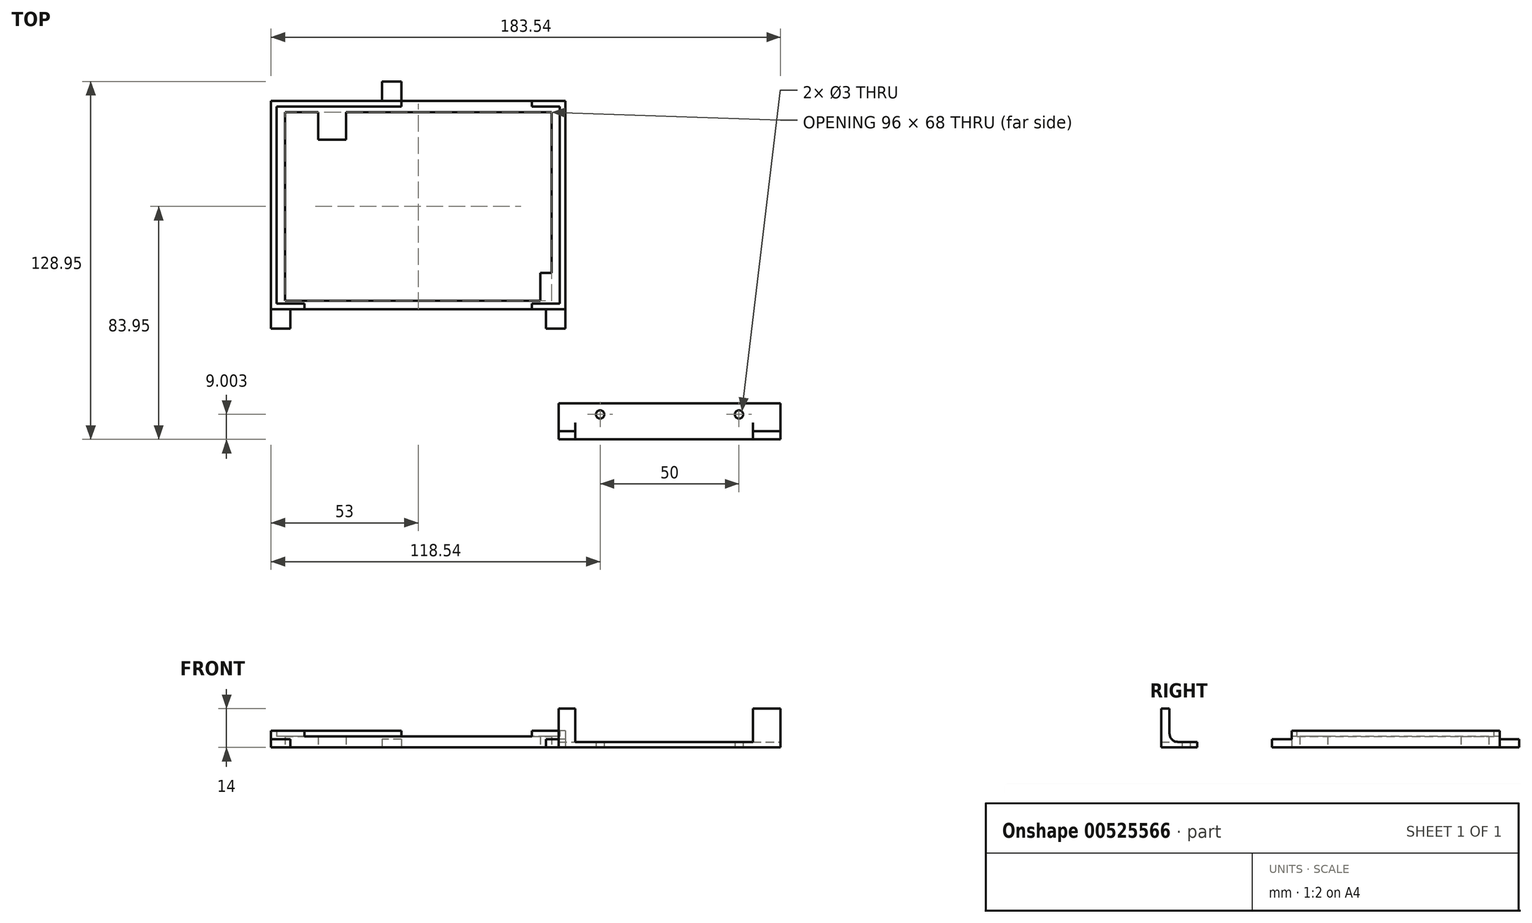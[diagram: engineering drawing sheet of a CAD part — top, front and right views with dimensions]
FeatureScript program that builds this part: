
annotation { "Feature Type Name" : "Feature", "Feature Type Description" : "" }
export const myFeature = defineFeature(function(context is Context, id is Id, definition is map)
    precondition{}
    {
        {
            var Q0;
            Q0=qCreatedBy(makeId("Top.planeOp"),FACE);
            var sketch = newSketch(context, id + "F0", { "sketchPlane" : qUnion([Q0])});
            skLineSegment(sketch, "E0.bottom", {"start": v(51, -35.5) * mm, "end": v(-51, -35.5) * mm});
            skLineSegment(sketch, "E0.top", {"start": v(51, 35.5) * mm, "end": v(-51, 35.5) * mm});
            skLineSegment(sketch, "E0.left", {"start": v(51, -35.5) * mm, "end": v(51, 35.5) * mm});
            skLineSegment(sketch, "E0.right", {"start": v(-51, -35.5) * mm, "end": v(-51, 35.5) * mm});
            skPoint(sketch, "E0.middle", {"position": v(0, 0) * mm});
            skLineSegment(sketch, "E1.bottom", {"start": v(53, -37.5) * mm, "end": v(-53, -37.5) * mm});
            skLineSegment(sketch, "E1.top", {"start": v(53, 37.5) * mm, "end": v(-53, 37.5) * mm});
            skLineSegment(sketch, "E1.left", {"start": v(53, -37.5) * mm, "end": v(53, 37.5) * mm});
            skLineSegment(sketch, "E1.right", {"start": v(-53, -37.5) * mm, "end": v(-53, 37.5) * mm});
            skSolve(sketch);
        }
        {
            var Q0;
            Q0=qSketchRegion(id+"F0",true);
            extrude(context, id + "F1", {"entities" : qUnion([Q0]), "depth" : 6 * mm, "offsetDistance" : 25 * mm});
        }
        {
            var Q0;
            Q0=makeQuery(id+"F1.opExtrude","CAP_FACE",FACE,{"disambiguationData":[OSD([sQuery(id+"F0.wireOp",EDGE,"E0.bottom"),sQuery(id+"F0.wireOp",EDGE,"E0.top"),sQuery(id+"F0.wireOp",EDGE,"E0.left"),sQuery(id+"F0.wireOp",EDGE,"E0.right"),sQuery(id+"F0.wireOp",EDGE,"E1.bottom"),sQuery(id+"F0.wireOp",EDGE,"E1.top"),sQuery(id+"F0.wireOp",EDGE,"E1.left"),sQuery(id+"F0.wireOp",EDGE,"E1.right")])],"isStart":true});
            var sketch = newSketch(context, id + "F2", { "sketchPlane" : qUnion([Q0])});
            skLineSegment(sketch, "E2.bottom", {"start": v(51, 35.5) * mm, "end": v(-51, 35.5) * mm});
            skLineSegment(sketch, "E2.top", {"start": v(51, -35.5) * mm, "end": v(-51, -35.5) * mm});
            skLineSegment(sketch, "E2.left", {"start": v(51, 35.5) * mm, "end": v(51, -35.5) * mm});
            skLineSegment(sketch, "E2.right", {"start": v(-51, 35.5) * mm, "end": v(-51, -35.5) * mm});
            skPoint(sketch, "E2.middle", {"position": v(0, 0) * mm});
            skLineSegment(sketch, "E3.bottom", {"start": v(-48, -33.5) * mm, "end": v(-36, -33.5) * mm});
            skLineSegment(sketch, "E3.top", {"start": v(-48, 34.5) * mm, "end": v(44, 34.5) * mm});
            skLineSegment(sketch, "E3.left", {"start": v(-48, -33.5) * mm, "end": v(-48, 34.5) * mm});
            skLineSegment(sketch, "E3.right", {"start": v(48, -33.5) * mm, "end": v(48, 24.5) * mm});
            skLineSegment(sketch, "E4", {"start": v(48, 24.5) * mm, "end": v(44, 24.5) * mm});
            skLineSegment(sketch, "E5", {"start": v(44, 24.5) * mm, "end": v(44, 34.5) * mm});
            skLineSegment(sketch, "E6", {"start": v(-36, -33.5) * mm, "end": v(-36, -23.5) * mm});
            skLineSegment(sketch, "E7", {"start": v(-36, -23.5) * mm, "end": v(-26, -23.5) * mm});
            skLineSegment(sketch, "E8", {"start": v(-26, -23.5) * mm, "end": v(-26, -33.5) * mm});
            skLineSegment(sketch, "E9.trimOffspring", {"start": v(-26, -33.5) * mm, "end": v(48, -33.5) * mm});
            skSolve(sketch);
        }
        {
            var Q0;
            Q0 = qSketchRegion(id + "F2", true);
            extrude(context, id + "F3", {"entities" : qUnion([Q0]), "operationType" : NewBodyOperationType.ADD, "oppositeDirection" : true, "depth" : 4 * mm, "offsetDistance" : 25 * mm});
        }
        {
            var Q0;
            Q0=makeQuery(id+"F1.opExtrude","CAP_FACE",FACE,{"disambiguationData":[OSD([sQuery(id+"F0.wireOp",EDGE,"E0.bottom"),sQuery(id+"F0.wireOp",EDGE,"E0.top"),sQuery(id+"F0.wireOp",EDGE,"E0.left"),sQuery(id+"F0.wireOp",EDGE,"E0.right"),sQuery(id+"F0.wireOp",EDGE,"E1.bottom"),sQuery(id+"F0.wireOp",EDGE,"E1.top"),sQuery(id+"F0.wireOp",EDGE,"E1.left"),sQuery(id+"F0.wireOp",EDGE,"E1.right")])],"isStart":false});
            var sketch = newSketch(context, id + "F4", { "sketchPlane" : qUnion([Q0])});
            skLineSegment(sketch, "E10.bottom", {"start": v(-41, -35.5) * mm, "end": v(41, -35.5) * mm});
            skLineSegment(sketch, "E10.top", {"start": v(-41, -37.5) * mm, "end": v(41, -37.5) * mm});
            skLineSegment(sketch, "E10.left", {"start": v(-41, -35.5) * mm, "end": v(-41, -37.5) * mm});
            skLineSegment(sketch, "E10.right", {"start": v(41, -35.5) * mm, "end": v(41, -37.5) * mm});
            skLineSegment(sketch, "E11.bottom", {"start": v(-6, 37.5) * mm, "end": v(41, 37.5) * mm});
            skLineSegment(sketch, "E11.top", {"start": v(-6, 35.5) * mm, "end": v(41, 35.5) * mm});
            skLineSegment(sketch, "E11.left", {"start": v(-6, 37.5) * mm, "end": v(-6, 35.5) * mm});
            skLineSegment(sketch, "E11.right", {"start": v(41, 37.5) * mm, "end": v(41, 35.5) * mm});
            skSolve(sketch);
        }
        {
            var Q0;
            Q0 = qSketchRegion(id + "F4", true);
            extrude(context, id + "F5", {"entities" : qUnion([Q0]), "operationType" : NewBodyOperationType.REMOVE, "oppositeDirection" : true, "depth" : 2 * mm, "offsetDistance" : 25 * mm});
        }
        {
            var Q0;
            Q0=makeQuery(id+"F3.boolean.opBoolean","MERGE",FACE,{"derivedFrom":[makeQuery(id+"F1.opExtrude","CAP_FACE",FACE,{"disambiguationData":[OSD([sQuery(id+"F0.wireOp",EDGE,"E0.bottom"),sQuery(id+"F0.wireOp",EDGE,"E0.top"),sQuery(id+"F0.wireOp",EDGE,"E0.left"),sQuery(id+"F0.wireOp",EDGE,"E0.right"),sQuery(id+"F0.wireOp",EDGE,"E1.bottom"),sQuery(id+"F0.wireOp",EDGE,"E1.top"),sQuery(id+"F0.wireOp",EDGE,"E1.left"),sQuery(id+"F0.wireOp",EDGE,"E1.right")])],"isStart":true}),makeQuery(id+"F3.opExtrude","CAP_FACE",FACE,{"disambiguationData":[OSD([sQuery(id+"F2.wireOp",EDGE,"E2.bottom"),sQuery(id+"F2.wireOp",EDGE,"E2.top"),sQuery(id+"F2.wireOp",EDGE,"E2.left"),sQuery(id+"F2.wireOp",EDGE,"E2.right"),sQuery(id+"F2.wireOp",EDGE,"E3.bottom"),sQuery(id+"F2.wireOp",EDGE,"E3.top"),sQuery(id+"F2.wireOp",EDGE,"E3.left"),sQuery(id+"F2.wireOp",EDGE,"E3.right"),sQuery(id+"F2.wireOp",EDGE,"E4"),sQuery(id+"F2.wireOp",EDGE,"E5"),sQuery(id+"F2.wireOp",EDGE,"E6"),sQuery(id+"F2.wireOp",EDGE,"E7"),sQuery(id+"F2.wireOp",EDGE,"E8"),sQuery(id+"F2.wireOp",EDGE,"E9.trimOffspring")])],"isStart":true})]});
            var sketch = newSketch(context, id + "F6", { "sketchPlane" : qUnion([Q0])});
            skLineSegment(sketch, "E12.bottom", {"start": v(53, 37.5) * mm, "end": v(46, 37.5) * mm});
            skLineSegment(sketch, "E12.top", {"start": v(53, 44.5) * mm, "end": v(46, 44.5) * mm});
            skLineSegment(sketch, "E12.left", {"start": v(53, 37.5) * mm, "end": v(53, 44.5) * mm});
            skLineSegment(sketch, "E12.right", {"start": v(46, 37.5) * mm, "end": v(46, 44.5) * mm});
            skCircle(sketch, "E13", {"center": v(49.5, 41) * mm, "radius": 1.5 * mm, "construction": true});
            skPoint(sketch, "E13.centerSnap0", {"position": v(46, 41) * mm});
            skPoint(sketch, "E13.centerSnap1", {"position": v(49.5, 37.5) * mm});
            skLineSegment(sketch, "E14.bottom", {"start": v(-53, 37.5) * mm, "end": v(-46, 37.5) * mm});
            skLineSegment(sketch, "E14.top", {"start": v(-53, 44.5) * mm, "end": v(-46, 44.5) * mm});
            skLineSegment(sketch, "E14.left", {"start": v(-53, 37.5) * mm, "end": v(-53, 44.5) * mm});
            skLineSegment(sketch, "E14.right", {"start": v(-46, 37.5) * mm, "end": v(-46, 44.5) * mm});
            skCircle(sketch, "E15", {"center": v(-49.5, 41) * mm, "radius": 1.5 * mm, "construction": true});
            skPoint(sketch, "E15.centerSnap0", {"position": v(-53, 41) * mm});
            skPoint(sketch, "E15.centerSnap1", {"position": v(-49.5, 37.5) * mm});
            skLineSegment(sketch, "E16.bottom", {"start": v(-13, -37.5) * mm, "end": v(-6, -37.5) * mm});
            skLineSegment(sketch, "E16.top", {"start": v(-13, -44.5) * mm, "end": v(-6, -44.5) * mm});
            skLineSegment(sketch, "E16.left", {"start": v(-13, -37.5) * mm, "end": v(-13, -44.5) * mm});
            skLineSegment(sketch, "E16.right", {"start": v(-6, -37.5) * mm, "end": v(-6, -44.5) * mm});
            skCircle(sketch, "E17", {"center": v(-9.5, -41) * mm, "radius": 1.5 * mm, "construction": true});
            skPoint(sketch, "E17.centerSnap0", {"position": v(-9.5, -44.5) * mm});
            skPoint(sketch, "E17.centerSnap1", {"position": v(-13, -41) * mm});
            skSolve(sketch);
        }
        {
            var Q0;
            Q0 = qSketchRegion(id + "F6", true);
            extrude(context, id + "F7", {"entities" : qUnion([Q0]), "operationType" : NewBodyOperationType.ADD, "oppositeDirection" : true, "depth" : 3 * mm, "offsetDistance" : 25 * mm});
        }
        {
            var Q0;
            Q0=qCreatedBy(makeId("Top.planeOp"),FACE);
            var sketch = newSketch(context, id + "F8", { "sketchPlane" : qUnion([Q0])});
            skLineSegment(sketch, "E18.bottom", {"start": v(130.54, -84.45) * mm, "end": v(50.54, -84.45) * mm});
            skLineSegment(sketch, "E18.top", {"start": v(130.54, -71.45) * mm, "end": v(50.54, -71.45) * mm});
            skLineSegment(sketch, "E18.left", {"start": v(130.54, -84.45) * mm, "end": v(130.54, -71.45) * mm});
            skLineSegment(sketch, "E18.right", {"start": v(50.54, -84.45) * mm, "end": v(50.54, -71.45) * mm});
            skPoint(sketch, "E18.middle", {"position": v(90.54, -77.95) * mm});
            skCircle(sketch, "E19", {"center": v(65.54, -75.45) * mm, "radius": 1.5 * mm});
            skCircle(sketch, "E20", {"center": v(115.54, -75.45) * mm, "radius": 1.5 * mm});
            skSolve(sketch);
        }
        {
            var Q0;
            Q0 = qSketchRegion(id + "F8", true);
            extrude(context, id + "F9", {"entities" : qUnion([Q0]), "depth" : 2 * mm, "offsetDistance" : 25 * mm});
        }
        {
            var Q0;
            Q0=makeQuery(id+"F9.opExtrude","SWEPT_FACE",FACE,{"disambiguationData":[OSD([sQuery(id+"F8.wireOp",EDGE,"E18.bottom")])]});
            var sketch = newSketch(context, id + "F10", { "sketchPlane" : qUnion([Q0])});
            skLineSegment(sketch, "E21.bottom", {"start": v(120.54, 0) * mm, "end": v(130.54, 0) * mm});
            skLineSegment(sketch, "E21.top", {"start": v(120.54, 14) * mm, "end": v(130.54, 14) * mm});
            skLineSegment(sketch, "E21.left", {"start": v(130.54, 0) * mm, "end": v(130.54, 14) * mm});
            skLineSegment(sketch, "E21.right", {"start": v(120.54, 0) * mm, "end": v(120.54, 14) * mm});
            skLineSegment(sketch, "E22.bottom", {"start": v(50.54, 0) * mm, "end": v(56.54, 0) * mm});
            skLineSegment(sketch, "E22.top", {"start": v(50.54, 14) * mm, "end": v(56.54, 14) * mm});
            skLineSegment(sketch, "E22.left", {"start": v(50.54, 0) * mm, "end": v(50.54, 14) * mm});
            skLineSegment(sketch, "E22.right", {"start": v(56.54, 0) * mm, "end": v(56.54, 14) * mm});
            skSolve(sketch);
        }
        {
            var Q0;
            Q0 = qSketchRegion(id + "F10", true);
            extrude(context, id + "F11", {"entities" : qUnion([Q0]), "operationType" : NewBodyOperationType.ADD, "oppositeDirection" : true, "depth" : 3 * mm, "offsetDistance" : 25 * mm});
        }
        {
            var Q0;
            Q0=makeQuery(id+"F11.boolean.opBoolean","INTERSECT",EDGE,{"derivedFrom":[makeQuery(id+"F9.opExtrude","CAP_FACE",FACE,{"disambiguationData":[OSD([sQuery(id+"F8.wireOp",EDGE,"E18.bottom"),sQuery(id+"F8.wireOp",EDGE,"E18.top"),sQuery(id+"F8.wireOp",EDGE,"E18.left"),sQuery(id+"F8.wireOp",EDGE,"E18.right"),sQuery(id+"F8.wireOp",EDGE,"E19"),sQuery(id+"F8.wireOp",EDGE,"E20")])],"isStart":false}),makeQuery(id+"F11.opExtrude","CAP_FACE",FACE,{"disambiguationData":[OSD([sQuery(id+"F10.wireOp",EDGE,"E22.bottom"),sQuery(id+"F10.wireOp",EDGE,"E22.top"),sQuery(id+"F10.wireOp",EDGE,"E22.left"),sQuery(id+"F10.wireOp",EDGE,"E22.right")])],"isStart":false})]});
            var Q1;
            Q1=makeQuery(id+"F11.boolean.opBoolean","INTERSECT",EDGE,{"derivedFrom":[makeQuery(id+"F9.opExtrude","CAP_FACE",FACE,{"disambiguationData":[OSD([sQuery(id+"F8.wireOp",EDGE,"E18.bottom"),sQuery(id+"F8.wireOp",EDGE,"E18.top"),sQuery(id+"F8.wireOp",EDGE,"E18.left"),sQuery(id+"F8.wireOp",EDGE,"E18.right"),sQuery(id+"F8.wireOp",EDGE,"E19"),sQuery(id+"F8.wireOp",EDGE,"E20")])],"isStart":false}),makeQuery(id+"F11.opExtrude","CAP_FACE",FACE,{"disambiguationData":[OSD([sQuery(id+"F10.wireOp",EDGE,"E21.bottom"),sQuery(id+"F10.wireOp",EDGE,"E21.top"),sQuery(id+"F10.wireOp",EDGE,"E21.left"),sQuery(id+"F10.wireOp",EDGE,"E21.right")])],"isStart":false})]});
            fillet(context, id + "F12", {"entities" : qUnion([Q0, Q1]), "radius" : 3 * mm, "tangentPropagation" : true, "allowEdgeOverflow" : false});
        }
    });
